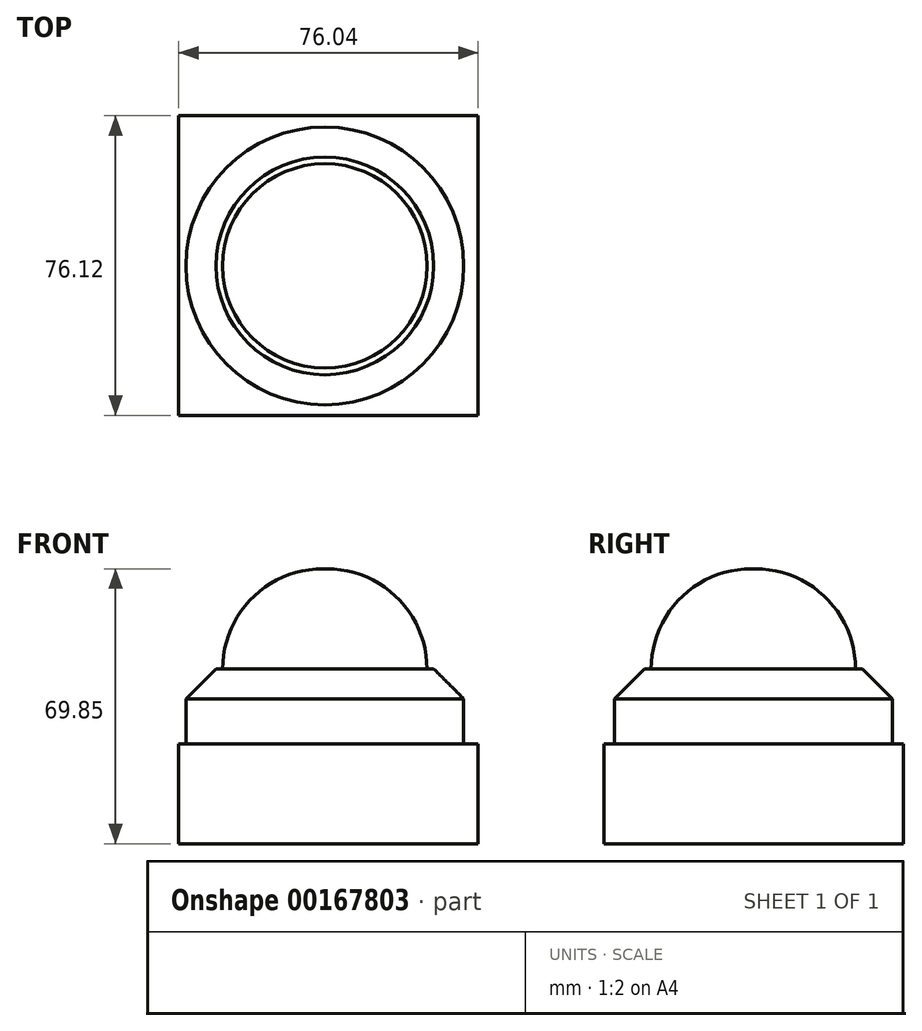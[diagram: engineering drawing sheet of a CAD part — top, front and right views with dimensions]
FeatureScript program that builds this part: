
annotation { "Feature Type Name" : "Feature", "Feature Type Description" : "" }
export const myFeature = defineFeature(function(context is Context, id is Id, definition is map)
    precondition{}
    {
        {
            var Q0;
            Q0=qCreatedBy(makeId("Top.planeOp"),FACE);
            var sketch = newSketch(context, id + "F0", { "sketchPlane" : qUnion([Q0])});
            skLineSegment(sketch, "E0.bottom", {"start": v(0, 0) * mm, "end": v(76.04, 0) * mm});
            skLineSegment(sketch, "E0.top", {"start": v(0, -76.12) * mm, "end": v(76.04, -76.12) * mm});
            skLineSegment(sketch, "E0.left", {"start": v(0, 0) * mm, "end": v(0, -76.12) * mm});
            skLineSegment(sketch, "E0.right", {"start": v(76.04, 0) * mm, "end": v(76.04, -76.12) * mm});
            skSolve(sketch);
        }
        {
            var Q0;
            Q0=makeQuery(id+"F0.imprint","IMPRINT",FACE,{"disambiguationData":[TD([[makeQuery(id+"F0.imprint","IMPRINT",EDGE,{"derivedFrom":sQuery(id+"F0.wireOp",EDGE,"E0.bottom")}),-1.0]])]});
            extrude(context, id + "F1", {"entities" : qUnion([Q0]), "depth" : 25.4 * mm});
        }
        {
            var Q0;
            Q0=makeQuery(id+"F1.opExtrude","CAP_FACE",FACE,{"disambiguationData":[OSD([sQuery(id+"F0.wireOp",EDGE,"E0.bottom"),sQuery(id+"F0.wireOp",EDGE,"E0.top"),sQuery(id+"F0.wireOp",EDGE,"E0.left"),sQuery(id+"F0.wireOp",EDGE,"E0.right")])],"isStart":false});
            var sketch = newSketch(context, id + "F2", { "sketchPlane" : qUnion([Q0])});
            skCircle(sketch, "E1", {"center": v(37.13, -38.16) * mm, "radius": 35.28 * mm});
            skSolve(sketch);
        }
        {
            var Q0;
            Q0=makeQuery(id+"F2.imprint","IMPRINT",FACE,{"disambiguationData":[TD([[makeQuery(id+"F2.imprint","IMPRINT",EDGE,{"derivedFrom":sQuery(id+"F2.wireOp",EDGE,"E1")}),1.0]])]});
            extrude(context, id + "F3", {"entities" : qUnion([Q0]), "depth" : 19.05 * mm});
        }
        {
            var Q0;
            Q0=makeQuery(id+"F3.opExtrude","CAP_FACE",FACE,{"disambiguationData":[OSD([sQuery(id+"F2.wireOp",EDGE,"E1")])],"isStart":false});
            var sketch = newSketch(context, id + "F4", { "sketchPlane" : qUnion([Q0])});
            skCircle(sketch, "E2", {"center": v(37.13, -38.16) * mm, "radius": 25.95 * mm});
            skSolve(sketch);
        }
        {
            var Q0;
            Q0=makeQuery(id+"F4.imprint","IMPRINT",FACE,{"disambiguationData":[TD([[makeQuery(id+"F4.imprint","IMPRINT",EDGE,{"derivedFrom":sQuery(id+"F4.wireOp",EDGE,"E2")}),1.0]])]});
            extrude(context, id + "F5", {"entities" : qUnion([Q0]), "depth" : 25.4 * mm});
        }
        {
            var Q0;
            Q0=makeQuery(id+"F5.opExtrude","CAP_FACE",FACE,{"disambiguationData":[OSD([sQuery(id+"F4.wireOp",EDGE,"E2")])],"isStart":false});
            fillet(context, id + "F6", {"entities" : qUnion([Q0]), "radius" : 25.4 * mm, "tangentPropagation" : true, "allowEdgeOverflow" : false});
        }
        {
            var Q0;
            Q0=makeQuery(id+"F3.opExtrude","CAP_EDGE",EDGE,{"disambiguationData":[OSD([sQuery(id+"F2.wireOp",EDGE,"E1")])],"isStart":false});
            chamfer(context, id + "F7", {"entities" : qUnion([Q0]), "width" : 7.62 * mm, "tangentPropagation" : true});
        }
    });
